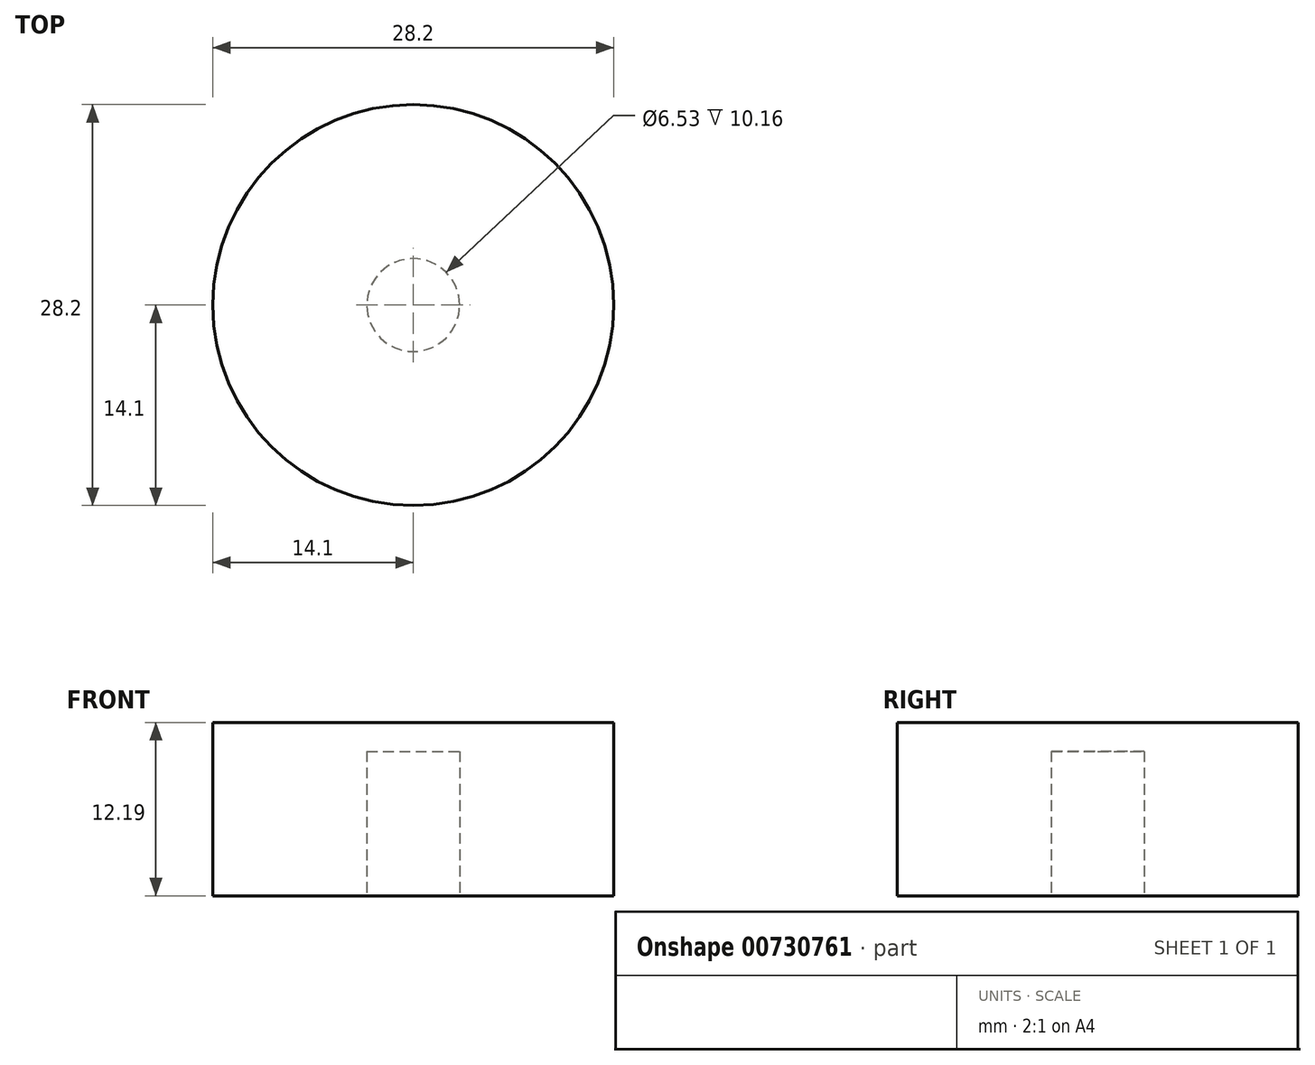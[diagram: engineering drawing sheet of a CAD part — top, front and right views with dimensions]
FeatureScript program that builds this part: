
annotation { "Feature Type Name" : "Feature", "Feature Type Description" : "" }
export const myFeature = defineFeature(function(context is Context, id is Id, definition is map)
    precondition{}
    {
        {
            var Q0;
            Q0=qCreatedBy(makeId("Top.planeOp"),FACE);
            var sketch = newSketch(context, id + "F0", { "sketchPlane" : qUnion([Q0])});
            skCircle(sketch, "E0", {"center": v(0, 0) * mm, "radius": 14.1 * mm});
            skSolve(sketch);
        }
        {
            var Q0;
            Q0=makeQuery(id+"F0.imprint","IMPRINT",FACE,{"disambiguationData":[TD([[makeQuery(id+"F0.imprint","IMPRINT",EDGE,{"derivedFrom":sQuery(id+"F0.wireOp",EDGE,"E0")}),1.0]])]});
            var Q1;
            Q1=sQuery(id+"F0.wireOp",EDGE,"E0");
            extrude(context, id + "F1", {"entities" : qUnion([Q0]), "surfaceEntities" : qUnion([Q1]), "depth" : 12.2 * mm, "offsetDistance" : 25.4 * mm});
        }
        {
            var Q0;
            Q0=makeQuery(id+"F1.opExtrude","CAP_FACE",FACE,{"disambiguationData":[OSD([sQuery(id+"F0.wireOp",EDGE,"E0")])],"isStart":true});
            var sketch = newSketch(context, id + "F2", { "sketchPlane" : qUnion([Q0])});
            skCircle(sketch, "E1", {"center": v(0, 0) * mm, "radius": 3.26 * mm});
            skSolve(sketch);
        }
        {
            var Q0;
            Q0=makeQuery(id+"F2.imprint","IMPRINT",FACE,{"disambiguationData":[TD([[makeQuery(id+"F2.imprint","IMPRINT",EDGE,{"derivedFrom":sQuery(id+"F2.wireOp",EDGE,"E1")}),1.0]])]});
            var Q1;
            Q1=sQuery(id+"F2.wireOp",EDGE,"E1");
            extrude(context, id + "F3", {"entities" : qUnion([Q0]), "operationType" : NewBodyOperationType.REMOVE, "surfaceEntities" : qUnion([Q1]), "oppositeDirection" : true, "depth" : 10.16 * mm, "offsetDistance" : 25.4 * mm});
        }
    });
